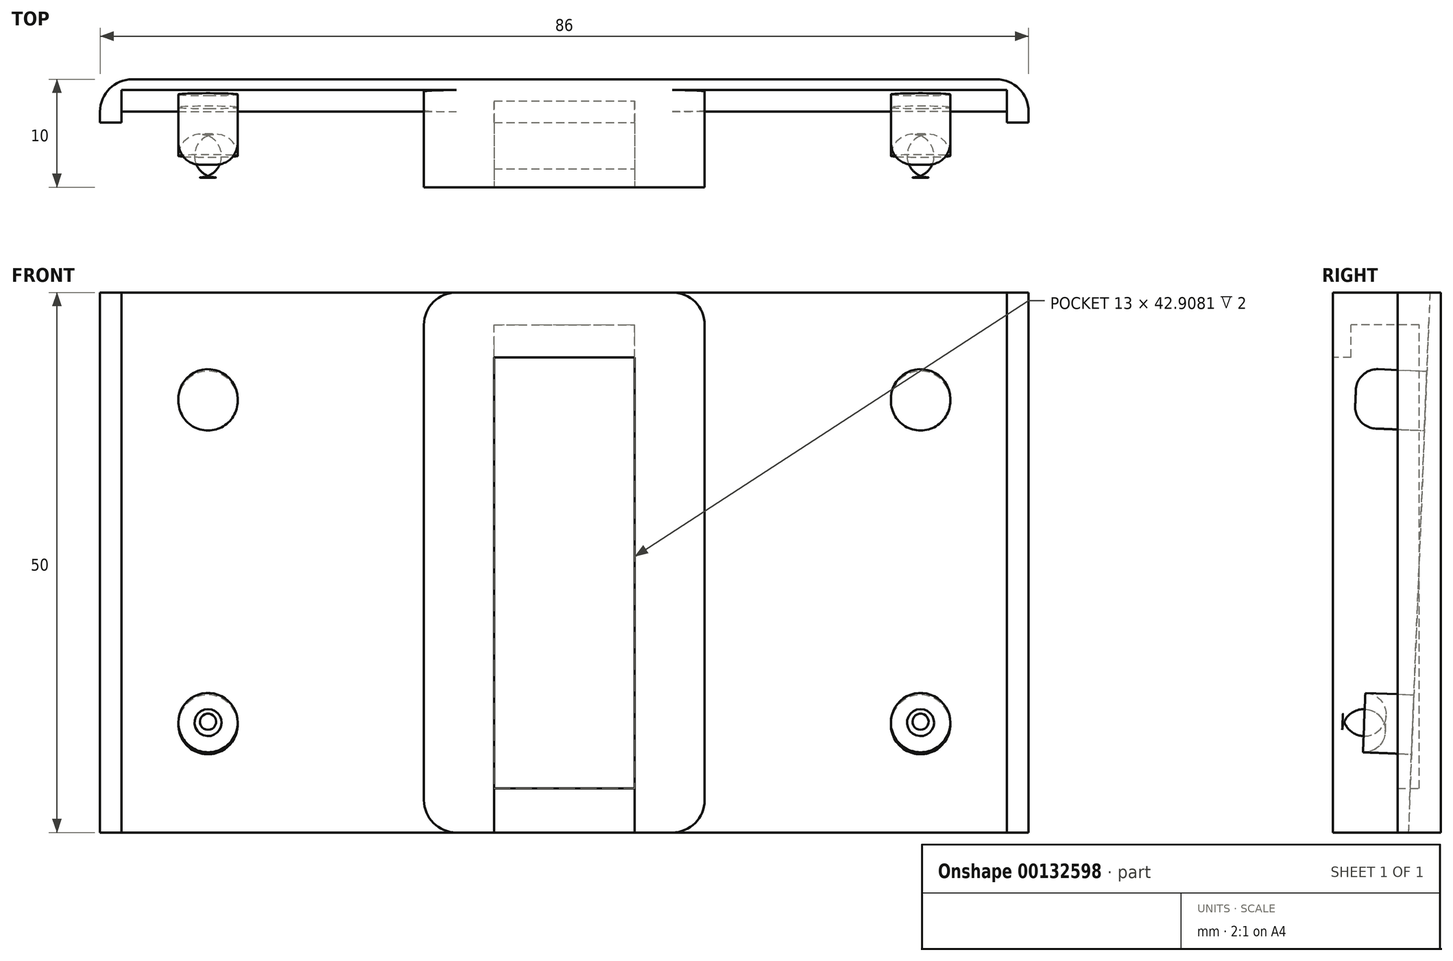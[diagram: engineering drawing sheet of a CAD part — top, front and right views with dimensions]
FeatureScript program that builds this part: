
annotation { "Feature Type Name" : "Feature", "Feature Type Description" : "" }
export const myFeature = defineFeature(function(context is Context, id is Id, definition is map)
    precondition{}
    {
        {
            var Q0;
            Q0=qCreatedBy(makeId("Front.planeOp"),FACE);
            var sketch = newSketch(context, id + "F0", { "sketchPlane" : qUnion([Q0])});
            skLineSegment(sketch, "E0.bottom", {"start": v(-85.27, 59.3) * mm, "end": v(0.73, 59.3) * mm});
            skLineSegment(sketch, "E0.top", {"start": v(-85.27, 9.3) * mm, "end": v(0.73, 9.3) * mm});
            skLineSegment(sketch, "E0.left", {"start": v(-85.27, 59.3) * mm, "end": v(-85.27, 9.3) * mm});
            skLineSegment(sketch, "E0.right", {"start": v(0.73, 59.3) * mm, "end": v(0.73, 9.3) * mm});
            skSolve(sketch);
        }
        {
            var Q0;
            Q0 = qSketchRegion(id + "F0", true);
            extrude(context, id + "F1", {"entities" : qUnion([Q0]), "depth" : 1 * mm});
        }
        {
            var Q0;
            Q0=makeQuery(id+"F1.opExtrude","CAP_FACE",FACE,{"disambiguationData":[OSD([sQuery(id+"F0.wireOp",EDGE,"E0.bottom"),sQuery(id+"F0.wireOp",EDGE,"E0.top"),sQuery(id+"F0.wireOp",EDGE,"E0.left"),sQuery(id+"F0.wireOp",EDGE,"E0.right")])],"isStart":false});
            var sketch = newSketch(context, id + "F2", { "sketchPlane" : qUnion([Q0])});
            skLineSegment(sketch, "E1.bottom", {"start": v(-55.27, 59.3) * mm, "end": v(-29.27, 59.3) * mm});
            skLineSegment(sketch, "E1.top", {"start": v(-55.27, 9.3) * mm, "end": v(-29.27, 9.3) * mm});
            skLineSegment(sketch, "E1.left", {"start": v(-55.27, 59.3) * mm, "end": v(-55.27, 9.3) * mm});
            skLineSegment(sketch, "E1.right", {"start": v(-29.27, 59.3) * mm, "end": v(-29.27, 9.3) * mm});
            skSolve(sketch);
        }
        {
            var Q0;
            Q0 = qSketchRegion(id + "F2", true);
            extrude(context, id + "F3", {"entities" : qUnion([Q0]), "operationType" : NewBodyOperationType.ADD, "depth" : 9 * mm});
        }
        {
            var Q0;
            Q0=makeQuery(id+"F3.opExtrude","CAP_FACE",FACE,{"disambiguationData":[OSD([sQuery(id+"F2.wireOp",EDGE,"E1.bottom"),sQuery(id+"F2.wireOp",EDGE,"E1.top"),sQuery(id+"F2.wireOp",EDGE,"E1.left"),sQuery(id+"F2.wireOp",EDGE,"E1.right")])],"isStart":false});
            var sketch = newSketch(context, id + "F4", { "sketchPlane" : qUnion([Q0])});
            skLineSegment(sketch, "E2.bottom", {"start": v(-48.77, 9.3) * mm, "end": v(-35.77, 9.3) * mm});
            skLineSegment(sketch, "E2.top", {"start": v(-48.77, 56.3) * mm, "end": v(-35.77, 56.3) * mm});
            skLineSegment(sketch, "E2.left", {"start": v(-48.77, 9.3) * mm, "end": v(-48.77, 56.3) * mm});
            skLineSegment(sketch, "E2.right", {"start": v(-35.77, 9.3) * mm, "end": v(-35.77, 56.3) * mm});
            skSolve(sketch);
        }
        {
            var Q0;
            Q0 = qSketchRegion(id + "F4", true);
            extrude(context, id + "F5", {"entities" : qUnion([Q0]), "operationType" : NewBodyOperationType.REMOVE, "oppositeDirection" : true, "depth" : 8 * mm});
        }
        {
            var Q0;
            Q0=makeQuery(id+"F5.boolean.opBoolean","COPY",FACE,{"derivedFrom":makeQuery(id+"F5.opExtrude","CAP_FACE",FACE,{"disambiguationData":[OSD([sQuery(id+"F4.wireOp",EDGE,"E2.bottom"),sQuery(id+"F4.wireOp",EDGE,"E2.top"),sQuery(id+"F4.wireOp",EDGE,"E2.left"),sQuery(id+"F4.wireOp",EDGE,"E2.right")])],"isStart":false})});
            var sketch = newSketch(context, id + "F6", { "sketchPlane" : qUnion([Q0])});
            skLineSegment(sketch, "E3.bottom", {"start": v(-48.77, 9.3) * mm, "end": v(-35.77, 9.3) * mm});
            skLineSegment(sketch, "E3.top", {"start": v(-48.77, 13.4) * mm, "end": v(-35.77, 13.4) * mm});
            skLineSegment(sketch, "E3.left", {"start": v(-48.77, 9.3) * mm, "end": v(-48.77, 13.4) * mm});
            skLineSegment(sketch, "E3.right", {"start": v(-35.77, 9.3) * mm, "end": v(-35.77, 13.4) * mm});
            skSolve(sketch);
        }
        {
            var Q0;
            Q0 = qSketchRegion(id + "F6", true);
            extrude(context, id + "F7", {"entities" : qUnion([Q0]), "operationType" : NewBodyOperationType.ADD, "depth" : 2 * mm});
        }
        {
            var Q0;
            Q0=makeQuery(id+"F5.boolean.opBoolean","COPY",FACE,{"derivedFrom":makeQuery(id+"F5.opExtrude","SWEPT_FACE",FACE,{"disambiguationData":[OSD([sQuery(id+"F4.wireOp",EDGE,"E2.top")])]})});
            var sketch = newSketch(context, id + "F8", { "sketchPlane" : qUnion([Q0])});
            skLineSegment(sketch, "E4.bottom", {"start": v(-48.77, 10) * mm, "end": v(-35.77, 10) * mm});
            skLineSegment(sketch, "E4.top", {"start": v(-48.77, 8.3) * mm, "end": v(-35.77, 8.3) * mm});
            skLineSegment(sketch, "E4.left", {"start": v(-48.77, 10) * mm, "end": v(-48.77, 8.3) * mm});
            skLineSegment(sketch, "E4.right", {"start": v(-35.77, 10) * mm, "end": v(-35.77, 8.3) * mm});
            skSolve(sketch);
        }
        {
            var Q0;
            Q0 = qSketchRegion(id + "F8", true);
            extrude(context, id + "F9", {"entities" : qUnion([Q0]), "operationType" : NewBodyOperationType.ADD, "depth" : 3 * mm});
        }
        {
            var Q0;
            Q0=makeQuery(id+"F3.opExtrude","SWEPT_FACE",FACE,{"disambiguationData":[OSD([sQuery(id+"F2.wireOp",EDGE,"E1.left")])]});
            var sketch = newSketch(context, id + "F10", { "sketchPlane" : qUnion([Q0])});
            skLineSegment(sketch, "E5.bottom", {"start": v(1, 59.3) * mm, "end": v(3, 59.3) * mm});
            skLineSegment(sketch, "E5.top", {"start": v(1, 9.3) * mm, "end": v(3, 9.3) * mm});
            skLineSegment(sketch, "E5.left", {"start": v(1, 59.3) * mm, "end": v(1, 9.3) * mm});
            skLineSegment(sketch, "E5.right", {"start": v(3, 59.3) * mm, "end": v(3, 9.3) * mm});
            skLineSegment(sketch, "E6", {"start": v(1, 59.3) * mm, "end": v(3, 9.3) * mm});
            skSolve(sketch);
        }
        {
            var Q0;
            Q0=makeQuery(id+"F10.imprint","IMPRINT",FACE,{"disambiguationData":[TD([[makeQuery(id+"F10.imprint","IMPRINT",EDGE,{"derivedFrom":sQuery(id+"F10.wireOp",EDGE,"E5.top")}),-1.0]])]});
            extrude(context, id + "F11", {"entities" : qUnion([Q0]), "operationType" : NewBodyOperationType.ADD, "depth" : 28 * mm});
        }
        {
            var Q0;
            Q0=makeQuery(id+"F3.opExtrude","SWEPT_FACE",FACE,{"disambiguationData":[OSD([sQuery(id+"F2.wireOp",EDGE,"E1.right")])]});
            var sketch = newSketch(context, id + "F12", { "sketchPlane" : qUnion([Q0])});
            skLineSegment(sketch, "E7.bottom", {"start": v(-3, 59.3) * mm, "end": v(-1, 59.3) * mm});
            skLineSegment(sketch, "E7.top", {"start": v(-3, 9.3) * mm, "end": v(-1, 9.3) * mm});
            skLineSegment(sketch, "E7.left", {"start": v(-3, 59.3) * mm, "end": v(-3, 9.3) * mm});
            skLineSegment(sketch, "E7.right", {"start": v(-1, 59.3) * mm, "end": v(-1, 9.3) * mm});
            skLineSegment(sketch, "E8", {"start": v(-3, 9.3) * mm, "end": v(-1, 59.3) * mm});
            skSolve(sketch);
        }
        {
            var Q0;
            Q0=makeQuery(id+"F12.imprint","IMPRINT",FACE,{"disambiguationData":[TD([[makeQuery(id+"F12.imprint","IMPRINT",EDGE,{"derivedFrom":sQuery(id+"F12.wireOp",EDGE,"E7.top")}),1.0]])]});
            extrude(context, id + "F13", {"entities" : qUnion([Q0]), "operationType" : NewBodyOperationType.ADD, "depth" : 28 * mm});
        }
        {
            var Q0;
            {var subQ0=sQuery(id+"F0.wireOp",EDGE,"E0.right");var subQ1=sQuery(id+"F0.wireOp",EDGE,"E0.top");var subQ2=sQuery(id+"F0.wireOp",EDGE,"E0.bottom");Q0=makeQuery(id+"F3.boolean.opBoolean","SPLIT",FACE,{"disambiguationData":[TD([makeQuery(id+"F1.opExtrude","SWEPT_FACE",FACE,{"disambiguationData":[OSD([subQ0])]})])],"derivedFrom":makeQuery(id+"F1.opExtrude","CAP_FACE",FACE,{"disambiguationData":[OSD([subQ2,subQ1,sQuery(id+"F0.wireOp",EDGE,"E0.left"),subQ0])],"isStart":false})});}
            var sketch = newSketch(context, id + "F14", { "sketchPlane" : qUnion([Q0])});
            skLineSegment(sketch, "E9.bottom", {"start": v(0.73, 9.3) * mm, "end": v(-1.27, 9.3) * mm});
            skLineSegment(sketch, "E9.top", {"start": v(0.73, 59.3) * mm, "end": v(-1.27, 59.3) * mm});
            skLineSegment(sketch, "E9.left", {"start": v(0.73, 9.3) * mm, "end": v(0.73, 59.3) * mm});
            skLineSegment(sketch, "E9.right", {"start": v(-1.27, 9.3) * mm, "end": v(-1.27, 59.3) * mm});
            skLineSegment(sketch, "E10.bottom", {"start": v(-83.27, 9.3) * mm, "end": v(-85.27, 9.3) * mm});
            skLineSegment(sketch, "E10.top", {"start": v(-83.27, 59.3) * mm, "end": v(-85.27, 59.3) * mm});
            skLineSegment(sketch, "E10.left", {"start": v(-83.27, 9.3) * mm, "end": v(-83.27, 59.3) * mm});
            skLineSegment(sketch, "E10.right", {"start": v(-85.27, 9.3) * mm, "end": v(-85.27, 59.3) * mm});
            skSolve(sketch);
        }
        {
            var Q0;
            Q0 = qSketchRegion(id + "F14", true);
            extrude(context, id + "F15", {"entities" : qUnion([Q0]), "operationType" : NewBodyOperationType.ADD, "depth" : 3 * mm});
        }
        {
            var Q0;
            Q0=makeQuery(id+"F1.opExtrude","CAP_EDGE",EDGE,{"disambiguationData":[OSD([sQuery(id+"F0.wireOp",EDGE,"E0.left")])],"isStart":true});
            var Q1;
            Q1=makeQuery(id+"F1.opExtrude","CAP_EDGE",EDGE,{"disambiguationData":[OSD([sQuery(id+"F0.wireOp",EDGE,"E0.right")])],"isStart":true});
            fillet(context, id + "F16", {"entities" : qUnion([Q0, Q1]), "radius" : 3 * mm, "tangentPropagation" : true, "allowEdgeOverflow" : false});
        }
        {
            var Q0;
            Q0=makeQuery(id+"F13.opExtrude","SWEPT_FACE",FACE,{"disambiguationData":[OSD([sQuery(id+"F12.wireOp",EDGE,"E8")])]});
            var sketch = newSketch(context, id + "F17", { "sketchPlane" : qUnion([Q0])});
            skCircle(sketch, "E11", {"center": v(-9.27, 49.18) * mm, "radius": 2.75 * mm});
            skCircle(sketch, "E12", {"center": v(-9.27, 19.18) * mm, "radius": 2.75 * mm});
            skCircle(sketch, "E13", {"center": v(-75.27, 49.18) * mm, "radius": 2.75 * mm});
            skCircle(sketch, "E14", {"center": v(-75.27, 19.18) * mm, "radius": 2.75 * mm});
            skSolve(sketch);
        }
        {
            var Q0;
            Q0 = qSketchRegion(id + "F17", true);
            extrude(context, id + "F18", {"entities" : qUnion([Q0]), "operationType" : NewBodyOperationType.ADD, "depth" : 6.5 * mm});
        }
        {
            var Q0;
            Q0=makeQuery(id+"F18.opExtrude","CAP_FACE",FACE,{"disambiguationData":[OSD([sQuery(id+"F17.wireOp",EDGE,"E13")])],"isStart":false});
            var Q1;
            Q1=makeQuery(id+"F18.opExtrude","CAP_FACE",FACE,{"disambiguationData":[OSD([sQuery(id+"F17.wireOp",EDGE,"E14")])],"isStart":false});
            var Q2;
            Q2=makeQuery(id+"F18.opExtrude","CAP_FACE",FACE,{"disambiguationData":[OSD([sQuery(id+"F17.wireOp",EDGE,"E11")])],"isStart":false});
            var Q3;
            Q3=makeQuery(id+"F18.opExtrude","CAP_FACE",FACE,{"disambiguationData":[OSD([sQuery(id+"F17.wireOp",EDGE,"E12")])],"isStart":false});
            fillet(context, id + "F19", {"entities" : qUnion([Q0, Q1, Q2, Q3]), "radius" : 2 * mm, "tangentPropagation" : true, "allowEdgeOverflow" : false});
        }
        {
            var Q0;
            Q0=makeQuery(id+"F3.opExtrude","SWEPT_EDGE",EDGE,{"disambiguationData":[OSD([sQuery(id+"F0.wireOp",EDGE,"E0.bottom"),sQuery(id+"F2.wireOp",EDGE,"E1.bottom"),sQuery(id+"F2.wireOp",EDGE,"E1.right")])]});
            var Q1;
            Q1=makeQuery(id+"F3.opExtrude","SWEPT_EDGE",EDGE,{"disambiguationData":[OSD([sQuery(id+"F0.wireOp",EDGE,"E0.bottom"),sQuery(id+"F2.wireOp",EDGE,"E1.bottom"),sQuery(id+"F2.wireOp",EDGE,"E1.left")])]});
            var Q2;
            Q2=makeQuery(id+"F3.opExtrude","SWEPT_EDGE",EDGE,{"disambiguationData":[OSD([sQuery(id+"F0.wireOp",EDGE,"E0.top"),sQuery(id+"F2.wireOp",EDGE,"E1.top"),sQuery(id+"F2.wireOp",EDGE,"E1.right")])]});
            var Q3;
            Q3=makeQuery(id+"F3.opExtrude","SWEPT_EDGE",EDGE,{"disambiguationData":[OSD([sQuery(id+"F0.wireOp",EDGE,"E0.top"),sQuery(id+"F2.wireOp",EDGE,"E1.top"),sQuery(id+"F2.wireOp",EDGE,"E1.left")])]});
            fillet(context, id + "F20", {"entities" : qUnion([Q0, Q1, Q2, Q3]), "radius" : 3 * mm, "tangentPropagation" : true, "allowEdgeOverflow" : false});
        }
    });
